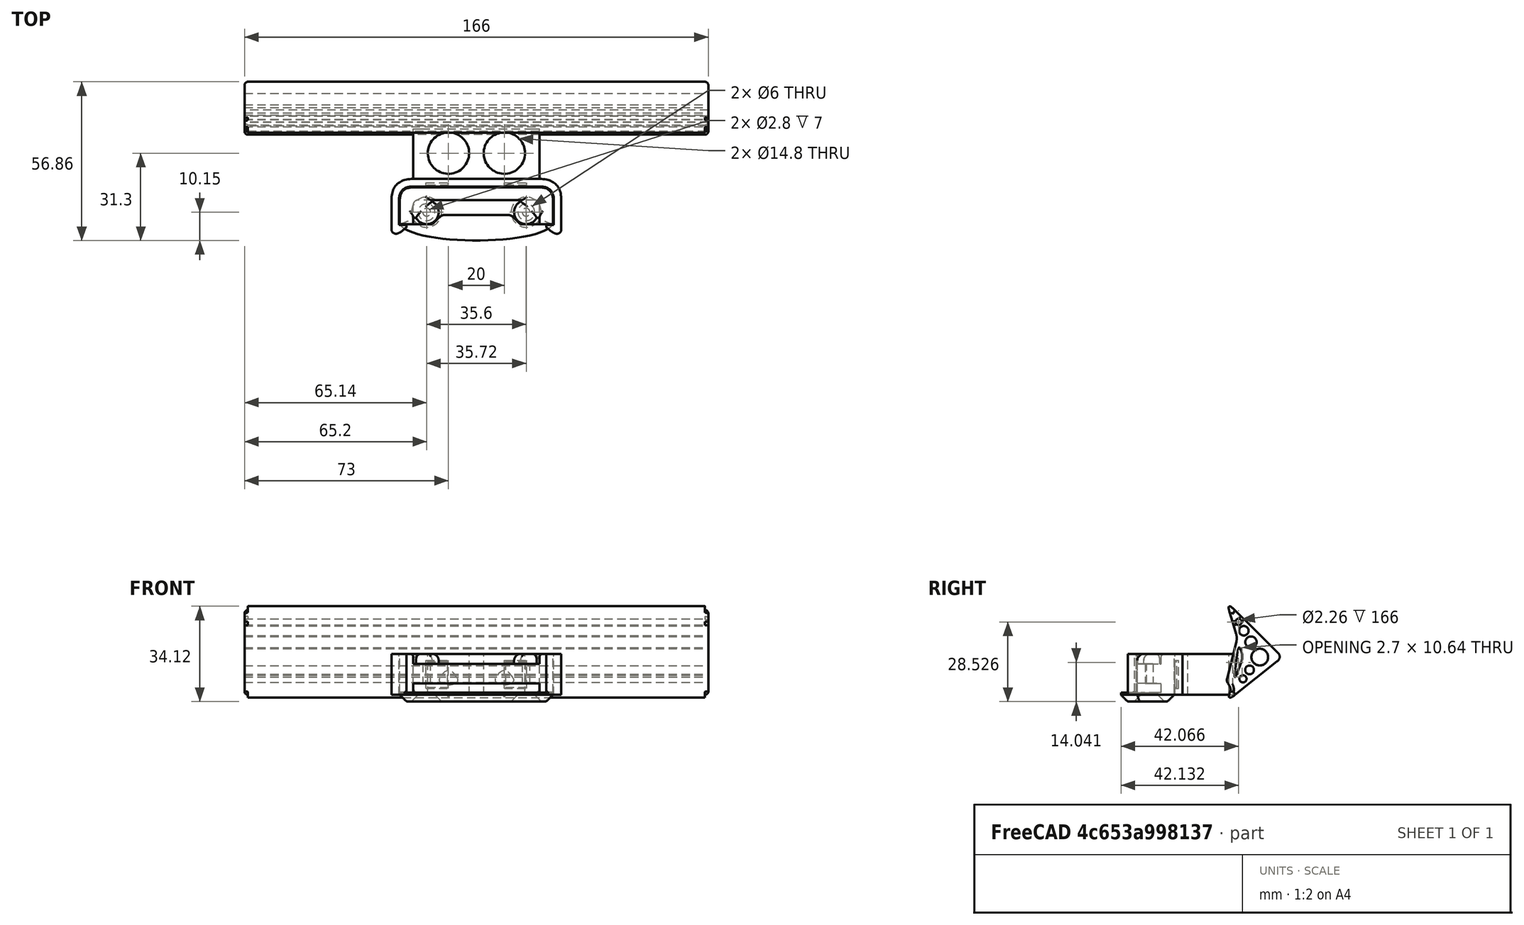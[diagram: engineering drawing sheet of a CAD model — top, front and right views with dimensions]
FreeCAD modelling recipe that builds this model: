
FCSTD DOCUMENT  (FreeCAD 0.21R0.20.1)
Label: 050
License: All rights reserved
LicenseURL: http://en.wikipedia.org/wiki/All_rights_reserved
objects: Sketcher::SketchObject×7, Part::Extrusion×7, Part::Fillet×7, Part::Box×5, Part::MultiFuse×5, Part::Cylinder×4, Part::Cut×4, Part::Chamfer×2
note: 41 computed .brp shape members not serialized (recipe doc carries the construction recipe); baked Part::Feature solids carry a one-line shape summary decoded from their .brp

FEATURE [Sketcher::SketchObject] Sketch  label="attatchmentPiece"
  FullyConstrained = true
  sketch-geometry (20):
    g0: LineSegment StartX=21.05 StartY=0 StartZ=0 EndX=21.05 EndY=-1 EndZ=0
    g1: LineSegment StartX=21.05 StartY=-1 StartZ=0 EndX=21.05 EndY=-4.3 EndZ=0
    g2: LineSegment StartX=-24.15 StartY=4.3 StartZ=0 EndX=21.05 EndY=4.3 EndZ=0
    g3: LineSegment StartX=21.05 StartY=0 StartZ=0 EndX=21.05 EndY=4.3 EndZ=0
    g4-g7: Circle x4 (B-spline internal-alignment scaffolding for g8; pole/knot coordinates omitted)
    g8: BSplineCurve PolesCount=4 KnotsCount=2 Degree=3 IsPeriodic=0
    g9: GeomPoint X=10.05 Y=-1 Z=0
    g10: GeomPoint X=14.55 Y=-4.3 Z=0
    g11: LineSegment StartX=10.05 StartY=-1 StartZ=0 EndX=-10.05 EndY=-1 EndZ=0
    g12: LineSegment StartX=14.55 StartY=-4.3 StartZ=0 EndX=21.05 EndY=-4.3 EndZ=0
    g13: LineSegment StartX=-24.15 StartY=4.3 StartZ=0 EndX=-24.15 EndY=-4.3 EndZ=0
    g14: LineSegment StartX=-13.15 StartY=-1 StartZ=0 EndX=-10.05 EndY=-1 EndZ=0
    g15: LineSegment StartX=-24.15 StartY=-4.3 StartZ=0 EndX=-19.35 EndY=-4.3 EndZ=0
    g16: LineSegment StartX=-19.35 StartY=-4.3 StartZ=0 EndX=-17.65 EndY=-4.3 EndZ=0
    g17: BSplineCurve PolesCount=4 KnotsCount=2 Degree=3 IsPeriodic=0
    g18: Circle CenterX=16.25 CenterY=0 CenterZ=0 NormalX=0 NormalY=0 NormalZ=1 AngleXU=0 Radius=1.4
    g19: Circle CenterX=-19.35 CenterY=0 CenterZ=0 NormalX=0 NormalY=0 NormalZ=1 AngleXU=0 Radius=1.4
  constraints (41):
    c: Vertical(g0)
    c: Coincident(g1,g0)
    c: Vertical(g1)
    c: Block(g0)
    c: Horizontal(g2)
    c: Vertical(g3)
    c: Coincident(g3,g2)
    c: Block(g2)
    c: Block(g3)
    c: Weight(g4) = 1
    c: Equal(g4,g5)
    c: Equal(g4,g6)
    c: Equal(g4,g7)
    c: InternalAlignment(g4-g7 -> g8) x4
    c: InternalAlignment(g9,g8)
    c: InternalAlignment(g10,g8)
    c: Block(g8)
    c: Coincident(g11,g8)
    c: Horizontal(g11)
    c: Coincident(g12,g8)
    c: Coincident(g12,g1)
    c: Horizontal(g12)
    c: Distance(g2) = 45.2
    c: Coincident(g13,g2)
    c: Vertical(g13)
    c: Horizontal(g14)
    c: Distance(g14) = 3.1
    c: Horizontal(g15)
    c: Block(g17)
    c: Coincident(g16,g15)
    c: Coincident(g16,g17)
    c: Horizontal(g16)
    c: Block(g16)
    c: Coincident(g17,g14)
    c: Block(g15)
    c: Block(g11)
    c: Block(g13)
    c: Distance(g15) = 4.8
    c: Distance(g16) = 1.7
    c: Block(g18)
    c: Block(g19)
FEATURE [Part::Extrusion] Extrude  label="attatchmentPiece001"
  Base = -> Sketch
  Dir = (0,0,1)
  DirMode = 2
  FaceMakerClass = Part::FaceMakerBullseye
  LengthFwd = 7
  LengthRev = 0
  Solid = true
  Symmetric = false
FEATURE [Sketcher::SketchObject] Sketch001  label="attatchmentPieceSurround"
  FullyConstrained = true
  sketch-geometry (18):
    g0: LineSegment StartX=25.85 StartY=-4.3 StartZ=0 EndX=21.05 EndY=-4.3 EndZ=0
    g1: LineSegment StartX=25.85 StartY=-4.3 StartZ=0 EndX=25.85 EndY=4.3 EndZ=0
    g2: LineSegment StartX=-21.05 StartY=8.9 StartZ=0 EndX=21.05 EndY=8.9 EndZ=0
    g3: Circle CenterX=21.05 CenterY=8.9 CenterZ=0 NormalX=0 NormalY=0 NormalZ=1 AngleXU=0 Radius=1
    g4: Circle CenterX=25.85 CenterY=8.9 CenterZ=0 NormalX=0 NormalY=0 NormalZ=1 AngleXU=0 Radius=1
    g5: Circle CenterX=25.85 CenterY=4.3 CenterZ=0 NormalX=0 NormalY=0 NormalZ=1 AngleXU=0 Radius=1
    g6: BSplineCurve PolesCount=3 KnotsCount=2 Degree=2 IsPeriodic=0
    g7: GeomPoint X=21.05 Y=8.9 Z=0
    g8: GeomPoint X=25.85 Y=4.3 Z=0
    g9: ArcOfCircle CenterX=19.45 CenterY=2.7 CenterZ=0 NormalX=0 NormalY=0 NormalZ=1 AngleXU=0 Radius=1.6 StartAngle=0 EndAngle=1.5708
    g10: LineSegment StartX=21.05 StartY=2.7 StartZ=0 EndX=21.05 EndY=-4.3 EndZ=0
    g11: BSplineCurve PolesCount=3 KnotsCount=2 Degree=2 IsPeriodic=0
    g12: LineSegment StartX=-28.95 StartY=-4.3 StartZ=0 EndX=-28.95 EndY=4.3 EndZ=0
    g13: LineSegment StartX=-24.15 StartY=-4.3 StartZ=0 EndX=-28.95 EndY=-4.3 EndZ=0
    g14: LineSegment StartX=-24.15 StartY=2.7 StartZ=0 EndX=-24.15 EndY=-4.3 EndZ=0
    g15: ArcOfCircle CenterX=-22.55 CenterY=2.7 CenterZ=0 NormalX=0 NormalY=0 NormalZ=1 AngleXU=0 Radius=1.6 StartAngle=1.5708 EndAngle=3.14159
    g16: LineSegment StartX=-24.15 StartY=8.9 StartZ=0 EndX=-21.05 EndY=8.9 EndZ=0
    g17: LineSegment StartX=-22.55 StartY=4.3 StartZ=0 EndX=19.45 EndY=4.3 EndZ=0
  constraints (38):
    c: Horizontal(g0)
    c: Vertical(g1)
    c: Coincident(g1,g0)
    c: Horizontal(g2)
    c: Distance(g2) = 42.1
    c: Block(g2)
    c: Coincident(g6,g2)
    c: Weight(g3) = 1
    c: Equal(g3,g4)
    c: Equal(g3,g5)
    c: Coincident(g6,g1)
    c: InternalAlignment(g3,g6)
    c: InternalAlignment(g4,g6)
    c: InternalAlignment(g5,g6)
    c: InternalAlignment(g7,g6)
    c: InternalAlignment(g8,g6)
    c: Block(g0)
    c: Block(g6)
    c: Block(g9)
    c: Coincident(g10,g9)
    c: Coincident(g10,g0)
    c: Vertical(g10)
    c: Horizontal(g13)
    c: Coincident(g12,g13)
    c: Vertical(g12)
    c: Coincident(g11,g12)
    c: Block(g12)
    c: Block(g11)
    c: Block(g15)
    c: Coincident(g14,g15)
    c: Coincident(g14,g13)
    c: Vertical(g14)
    c: Coincident(g16,g11)
    c: Coincident(g16,g2)
    c: Horizontal(g16)
    c: Coincident(g17,g15)
    c: Coincident(g17,g9)
    c: Horizontal(g17)
FEATURE [Part::Extrusion] Extrude001  label="attatchmentPieceSurround001"
  Base = -> Sketch001
  Dir = (0,0,1)
  DirMode = 2
  FaceMakerClass = Part::FaceMakerBullseye
  LengthFwd = 14.7
  LengthRev = 0
  Placement = pos=(0,0,-4.1) rot=(0,0,1;0rad)
  Solid = true
  Symmetric = false
FEATURE [Sketcher::SketchObject] Sketch002  label="attatchmentPieceEndScrewHoleCaps"
  FullyConstrained = true
  sketch-geometry (10):
    g0: ArcOfCircle CenterX=16.25 CenterY=0 CenterZ=0 NormalX=0 NormalY=0 NormalZ=1 AngleXU=0 Radius=4.3 StartAngle=2.05456 EndAngle=5.79942
    g1: LineSegment StartX=14.25 StartY=3.80657 StartZ=0 EndX=14.25 EndY=6 EndZ=0
    g2: LineSegment StartX=20.0566 StartY=-2 StartZ=0 EndX=22.25 EndY=-2 EndZ=0
    g3: LineSegment StartX=22.25 StartY=-2 StartZ=0 EndX=22.25 EndY=6 EndZ=0
    g4: LineSegment StartX=14.25 StartY=6 StartZ=0 EndX=22.25 EndY=6 EndZ=0
    g5: LineSegment StartX=-25.35 StartY=-2 StartZ=0 EndX=-25.35 EndY=6 EndZ=0
    g6: LineSegment StartX=-25.35 StartY=-2 StartZ=0 EndX=-23.1566 EndY=-2 EndZ=0
    g7: LineSegment StartX=-17.35 StartY=6 StartZ=0 EndX=-25.35 EndY=6 EndZ=0
    g8: LineSegment StartX=-17.35 StartY=3.80657 StartZ=0 EndX=-17.35 EndY=6 EndZ=0
    g9: ArcOfCircle CenterX=-19.35 CenterY=0 CenterZ=0 NormalX=0 NormalY=0 NormalZ=1 AngleXU=0 Radius=4.3 StartAngle=3.62536 EndAngle=7.37022
  constraints (25):
    c: Block(g0)
    c: Vertical(g1)
    c: Horizontal(g2)
    c: Coincident(g3,g2)
    c: Vertical(g3)
    c: Coincident(g4,g1)
    c: Horizontal(g4)
    c: Coincident(g3,g4)
    c: Block(g4)
    c: Block(g3)
    c: Coincident(g0,g1)
    c: Coincident(g0,g2)
    c: Block(g1)
    c: Block(g9)
    c: Horizontal(g6)
    c: Vertical(g8)
    c: Coincident(g7,g8)
    c: Horizontal(g7)
    c: Coincident(g5,g6)
    c: Vertical(g5)
    c: Coincident(g5,g7)
    c: Block(g7)
    c: Block(g5)
    c: Coincident(g9,g6)
    c: Coincident(g9,g8)
FEATURE [Part::Extrusion] Extrude002  label="attatchmentPieceEndScrewHoleCaps001"
  Base = -> Sketch002
  Dir = (0,0,1)
  DirMode = 2
  FaceMakerClass = Part::FaceMakerBullseye
  LengthFwd = 3.6
  LengthRev = 0
  Placement = pos=(0,0,7) rot=(0,0,1;0rad)
  Solid = true
  Symmetric = false
FEATURE [Sketcher::SketchObject] Sketch003  label="mainBumpperPieceAttatchment"
  FullyConstrained = true
  sketch-geometry (42):
    g0: Circle CenterX=28.85 CenterY=4.3 CenterZ=0 NormalX=0 NormalY=0 NormalZ=1 AngleXU=0 Radius=1
    g1: Circle CenterX=28.85 CenterY=11.9 CenterZ=0 NormalX=0 NormalY=0 NormalZ=1 AngleXU=0 Radius=1
    g2: Circle CenterX=21.05 CenterY=11.9 CenterZ=0 NormalX=0 NormalY=0 NormalZ=1 AngleXU=0 Radius=1
    g3: BSplineCurve PolesCount=3 KnotsCount=2 Degree=2 IsPeriodic=0
    g4: GeomPoint X=28.85 Y=4.3 Z=0
    g5: GeomPoint X=21.05 Y=11.9 Z=0
    g6: LineSegment StartX=-21.05 StartY=11.9 StartZ=0 EndX=21.05 EndY=11.9 EndZ=0
    g7: LineSegment StartX=28.85 StartY=4.3 StartZ=0 EndX=28.85 EndY=-4.3 EndZ=0
    g8: Circle CenterX=21.05 CenterY=9.2 CenterZ=0 NormalX=0 NormalY=0 NormalZ=1 AngleXU=0 Radius=1
    g9: Circle CenterX=26.15 CenterY=9.2 CenterZ=0 NormalX=0 NormalY=0 NormalZ=1 AngleXU=0 Radius=1
    g10: Circle CenterX=26.15 CenterY=4.3 CenterZ=0 NormalX=0 NormalY=0 NormalZ=1 AngleXU=0 Radius=1
    g11: BSplineCurve PolesCount=3 KnotsCount=2 Degree=2 IsPeriodic=0
    g12: GeomPoint X=21.05 Y=9.2 Z=0
    g13: GeomPoint X=26.15 Y=4.3 Z=0
    g14: LineSegment StartX=-21.05 StartY=9.2 StartZ=0 EndX=21.05 EndY=9.2 EndZ=0
    g15: LineSegment StartX=26.15 StartY=-4.3 StartZ=0 EndX=26.15 EndY=4.3 EndZ=0
    g16: LineSegment StartX=26.15 StartY=-4.3 StartZ=0 EndX=26.15 EndY=-4.6 EndZ=0
    g17: LineSegment StartX=23.45 StartY=-4.6 StartZ=0 EndX=26.15 EndY=-4.6 EndZ=0
    g18: LineSegment StartX=28.85 StartY=-4.3 StartZ=0 EndX=28.85 EndY=-7.9 EndZ=0
    g19: LineSegment StartX=23.45 StartY=-4.6 StartZ=0 EndX=23.45 EndY=-5.3 EndZ=0
    g20: Circle CenterX=28.85 CenterY=-7.9 CenterZ=0 NormalX=0 NormalY=0 NormalZ=1 AngleXU=0 Radius=1
    g21: Circle CenterX=26.15 CenterY=-8.2 CenterZ=0 NormalX=0 NormalY=0 NormalZ=1 AngleXU=0 Radius=1
    g22: Circle CenterX=23.45 CenterY=-5.3 CenterZ=0 NormalX=0 NormalY=0 NormalZ=1 AngleXU=0 Radius=1
    g23: BSplineCurve PolesCount=3 KnotsCount=2 Degree=2 IsPeriodic=0
    g24: GeomPoint X=28.85 Y=-7.9 Z=0
    g25: GeomPoint X=23.45 Y=-5.3 Z=0
    g26: LineSegment StartX=-21.05 StartY=9.2 StartZ=0 EndX=-24.15 EndY=9.2 EndZ=0
    g27: BSplineCurve PolesCount=3 KnotsCount=2 Degree=2 IsPeriodic=0
    g28: LineSegment StartX=-29.25 StartY=-4.3 StartZ=0 EndX=-29.25 EndY=-4.6 EndZ=0
    g29: LineSegment StartX=-29.25 StartY=-4.6 StartZ=0 EndX=-26.55 EndY=-4.6 EndZ=0
    g30: LineSegment StartX=-31.95 StartY=-4.3 StartZ=0 EndX=-31.95 EndY=-7.9 EndZ=0
    g31: LineSegment StartX=-26.55 StartY=-4.6 StartZ=0 EndX=-26.55 EndY=-5.3 EndZ=0
    g32: Circle CenterX=-31.95 CenterY=-7.9 CenterZ=0 NormalX=0 NormalY=0 NormalZ=1 AngleXU=0 Radius=1
    g33: Circle CenterX=-29.25 CenterY=-8.2 CenterZ=0 NormalX=0 NormalY=0 NormalZ=1 AngleXU=0 Radius=1
    g34: Circle CenterX=-26.55 CenterY=-5.3 CenterZ=0 NormalX=0 NormalY=0 NormalZ=1 AngleXU=0 Radius=1
    g35: BSplineCurve PolesCount=3 KnotsCount=2 Degree=2 IsPeriodic=0
    g36: GeomPoint X=-31.95 Y=-7.9 Z=0
    g37: GeomPoint X=-26.55 Y=-5.3 Z=0
    g38: LineSegment StartX=-31.95 StartY=4.3 StartZ=0 EndX=-31.95 EndY=-4.3 EndZ=0
    g39: LineSegment StartX=-29.25 StartY=-4.3 StartZ=0 EndX=-29.25 EndY=4.3 EndZ=0
    g40: BSplineCurve PolesCount=3 KnotsCount=2 Degree=2 IsPeriodic=0
    g41: LineSegment StartX=-21.05 StartY=11.9 StartZ=0 EndX=-24.15 EndY=11.9 EndZ=0
  constraints (78):
    c: Weight(g0) = 1
    c: Equal(g0,g1)
    c: Equal(g0,g2)
    c: InternalAlignment(g0,g3)
    c: InternalAlignment(g1,g3)
    c: InternalAlignment(g2,g3)
    c: InternalAlignment(g4,g3)
    c: InternalAlignment(g5,g3)
    c: Block(g3)
    c: Horizontal(g6)
    c: Vertical(g7)
    c: Block(g7)
    c: Block(g6)
    c: Weight(g8) = 1
    c: Equal(g8,g9)
    c: Equal(g8,g10)
    c: InternalAlignment(g8,g11)
    c: InternalAlignment(g9,g11)
    c: InternalAlignment(g10,g11)
    c: InternalAlignment(g12,g11)
    c: InternalAlignment(g13,g11)
    c: Horizontal(g14)
    c: Vertical(g15)
    c: Block(g11)
    c: Block(g15)
    c: Block(g14)
    c: Coincident(g16,g15)
    c: Vertical(g16)
    c: Distance(g16) = 0.3
    c: Horizontal(g17)
    c: Coincident(g17,g16)
    c: Coincident(g18,g7)
    c: Vertical(g18)
    c: Distance(g18) = 3.6
    c: Vertical(g19)
    c: Coincident(g19,g17)
    c: Coincident(g23,g18)
    c: Weight(g20) = 1
    c: Equal(g20,g21)
    c: Equal(g20,g22)
    c: Coincident(g23,g19)
    c: InternalAlignment(g20,g23)
    c: InternalAlignment(g21,g23)
    c: InternalAlignment(g22,g23)
    c: InternalAlignment(g24,g23)
    c: InternalAlignment(g25,g23)
    c: Block(g23)
    c: Horizontal(g26)
    c: Distance(g26) = 3.1
    c: Block(g27)
    c: Vertical(g38)
    c: Block(g38)
    c: Vertical(g39)
    c: Block(g40)
    c: Block(g39)
    c: Vertical(g28)
    c: Coincident(g28,g39)
    c: Coincident(g29,g28)
    c: Horizontal(g29)
    c: Vertical(g30)
    c: Coincident(g30,g38)
    c: Coincident(g31,g29)
    c: Vertical(g31)
    c: Coincident(g35,g30)
    c: Equal(g32,g33)
    c: Equal(g32,g34)
    c: Coincident(g35,g31)
    c: InternalAlignment(g32,g35)
    c: InternalAlignment(g33,g35)
    c: InternalAlignment(g34,g35)
    c: InternalAlignment(g36,g35)
    c: InternalAlignment(g37,g35)
    c: Block(g35)
    c: Coincident(g40,g26)
    c: Block(g29)
    c: Horizontal(g41)
    c: Equal(g26,g41) = 3.1
    c: Coincident(g41,g6)
FEATURE [Part::Box] Box  label="bumpperExtension"
  AttacherType = Attacher::AttachEngine3D
  Height = 14.7
  Length = 45.2
  Placement = pos=(-24.15,11.9,-4.1) rot=(0,0,1;0rad)
  Width = 18
FEATURE [Sketcher::SketchObject] Sketch004  label="bumpperMain"
  FullyConstrained = true
  Placement = pos=(0,0,0) rot=(0.57735,0.57735,0.57735;2.0944rad)
  sketch-geometry (62):
    g0: Circle CenterX=-3.12329 CenterY=2.49901 CenterZ=0 NormalX=0 NormalY=0 NormalZ=1 AngleXU=0 Radius=1
    g1: Circle CenterX=0 CenterY=0 CenterZ=0 NormalX=0 NormalY=0 NormalZ=1 AngleXU=0 Radius=1
    g2: Circle CenterX=-1.35243 CenterY=3.60648 CenterZ=0 NormalX=0 NormalY=0 NormalZ=1 AngleXU=0 Radius=1
    g3: BSplineCurve PolesCount=3 KnotsCount=2 Degree=2 IsPeriodic=0
    g4: GeomPoint X=-3.12329 Y=2.49901 Z=0
    g5: GeomPoint X=-1.35243 Y=3.60648 Z=0
    g6: Circle CenterX=-2.83953 CenterY=33.0261 CenterZ=0 NormalX=0 NormalY=0 NormalZ=1 AngleXU=0 Radius=1
    g7: Circle CenterX=0 CenterY=35.8434 CenterZ=0 NormalX=0 NormalY=0 NormalZ=1 AngleXU=0 Radius=1
    g8: Circle CenterX=-1.15771 CenterY=32.0146 CenterZ=0 NormalX=0 NormalY=0 NormalZ=1 AngleXU=0 Radius=1
    g9: BSplineCurve PolesCount=3 KnotsCount=2 Degree=2 IsPeriodic=0
    g10: GeomPoint X=-2.83953 Y=33.0261 Z=0
    g11: GeomPoint X=-1.15771 Y=32.0146 Z=0
    g12: Circle CenterX=-18.2963 CenterY=17.6904 CenterZ=0 NormalX=0 NormalY=0 NormalZ=1 AngleXU=0 Radius=1
    g13: Circle CenterX=-20 CenterY=16 CenterZ=0 NormalX=0 NormalY=0 NormalZ=1 AngleXU=0 Radius=1
    g14: Circle CenterX=-18.1259 CenterY=14.5008 CenterZ=0 NormalX=0 NormalY=0 NormalZ=1 AngleXU=0 Radius=1
    g15: BSplineCurve PolesCount=3 KnotsCount=2 Degree=2 IsPeriodic=0
    g16: GeomPoint X=-18.2963 Y=17.6904 Z=0
    g17: GeomPoint X=-18.1259 Y=14.5008 Z=0
    g18: LineSegment StartX=-18.2963 StartY=17.6904 StartZ=0 EndX=-2.83953 EndY=33.0261 EndZ=0
    g19: LineSegment StartX=-18.1259 StartY=14.5008 StartZ=0 EndX=-3.12329 EndY=2.49901 EndZ=0
    g20: Circle CenterX=-11.9527 CenterY=16 CenterZ=0 NormalX=0 NormalY=0 NormalZ=1 AngleXU=0 Radius=2.99582
    g21: Circle CenterX=-8.803 CenterY=21.3731 CenterZ=0 NormalX=0 NormalY=0 NormalZ=1 AngleXU=0 Radius=2.03939
    g22: Circle CenterX=-6.23123 CenterY=25.4475 CenterZ=0 NormalX=0 NormalY=0 NormalZ=1 AngleXU=0 Radius=1.69309
    g23: Circle CenterX=-4.38186 CenterY=28.6261 CenterZ=0 NormalX=0 NormalY=0 NormalZ=1 AngleXU=0 Radius=1.13029
    g24: Circle CenterX=-8.28033 CenterY=11.4296 CenterZ=0 NormalX=0 NormalY=0 NormalZ=1 AngleXU=0 Radius=1.57213
    g25: Circle CenterX=-5.93972 CenterY=8.22213 CenterZ=0 NormalX=0 NormalY=0 NormalZ=1 AngleXU=0 Radius=1.28743
    g26: Circle CenterX=-3.47023 CenterY=24.3665 CenterZ=0 NormalX=0 NormalY=0 NormalZ=1 AngleXU=0 Radius=1
    g27: Circle CenterX=-3.90437 CenterY=22.9307 CenterZ=0 NormalX=0 NormalY=0 NormalZ=1 AngleXU=0 Radius=1
    g28: Circle CenterX=-3.53772 CenterY=21.4762 CenterZ=0 NormalX=0 NormalY=0 NormalZ=1 AngleXU=0 Radius=1
    g29: BSplineCurve PolesCount=3 KnotsCount=2 Degree=2 IsPeriodic=0
    g30: GeomPoint X=-3.47023 Y=24.3665 Z=0
    g31: GeomPoint X=-3.53772 Y=21.4762 Z=0
    g32: LineSegment StartX=-1.15771 StartY=32.0146 StartZ=0 EndX=-3.47023 EndY=24.3665 EndZ=0
    g33: Circle CenterX=-5.41867 CenterY=17.9226 CenterZ=0 NormalX=0 NormalY=0 NormalZ=1 AngleXU=0 Radius=1
    g34: Circle CenterX=-6 CenterY=16 CenterZ=0 NormalX=0 NormalY=0 NormalZ=1 AngleXU=0 Radius=1
    g35: Circle CenterX=-5.22753 CenterY=13.9401 CenterZ=0 NormalX=0 NormalY=0 NormalZ=1 AngleXU=0 Radius=1
    g36: BSplineCurve PolesCount=3 KnotsCount=2 Degree=2 IsPeriodic=0
    g37: GeomPoint X=-5.41867 Y=17.9226 Z=0
    g38: GeomPoint X=-5.22753 Y=13.9401 Z=0
    g39: Circle CenterX=-3.98946 CenterY=10.6386 CenterZ=0 NormalX=0 NormalY=0 NormalZ=1 AngleXU=0 Radius=1
    g40: Circle CenterX=-2.58497 CenterY=6.89324 CenterZ=0 NormalX=0 NormalY=0 NormalZ=1 AngleXU=0 Radius=1
    g41: Circle CenterX=-3.11001 CenterY=10.8586 CenterZ=0 NormalX=0 NormalY=0 NormalZ=1 AngleXU=0 Radius=1
    g42: BSplineCurve PolesCount=3 KnotsCount=2 Degree=2 IsPeriodic=0
    g43: GeomPoint X=-3.98946 Y=10.6386 Z=0
    g44: GeomPoint X=-3.11001 Y=10.8586 Z=0
    g45: Circle CenterX=-1.35243 CenterY=3.60648 CenterZ=0 NormalX=0 NormalY=0 NormalZ=1 AngleXU=0 Radius=1
    g46: Circle CenterX=-1.76142 CenterY=4.69712 CenterZ=0 NormalX=0 NormalY=0 NormalZ=1 AngleXU=0 Radius=1
    g47: Circle CenterX=-1.05937 CenterY=5.79125 CenterZ=0 NormalX=0 NormalY=0 NormalZ=1 AngleXU=0 Radius=1
    g48: BSplineCurve PolesCount=3 KnotsCount=2 Degree=2 IsPeriodic=0
    g49: GeomPoint X=-1.35243 Y=3.60648 Z=0
    g50: GeomPoint X=-1.05937 Y=5.79125 Z=0
    g51: Circle CenterX=-0.519336 CenterY=6.6329 CenterZ=0 NormalX=0 NormalY=0 NormalZ=1 AngleXU=0 Radius=1
    g52: Circle CenterX=0 CenterY=7.44228 CenterZ=0 NormalX=0 NormalY=0 NormalZ=1 AngleXU=0 Radius=1
    g53: Circle CenterX=-0.244436 CenterY=8.41194 CenterZ=0 NormalX=0 NormalY=0 NormalZ=1 AngleXU=0 Radius=1
    g54: BSplineCurve PolesCount=3 KnotsCount=2 Degree=2 IsPeriodic=0
    g55: GeomPoint X=-0.519336 Y=6.6329 Z=0
    g56: GeomPoint X=-0.244436 Y=8.41194 Z=0
    g57: LineSegment StartX=-3.53772 StartY=21.4762 StartZ=0 EndX=-0.244436 EndY=8.41194 EndZ=0
    g58: LineSegment StartX=-5.22753 StartY=13.9401 StartZ=0 EndX=-3.98946 EndY=10.6386 EndZ=0
    g59: LineSegment StartX=-1.05937 StartY=5.79125 StartZ=0 EndX=-0.519336 EndY=6.6329 EndZ=0
    g60: BSplineCurve PolesCount=3 KnotsCount=2 Degree=2 IsPeriodic=0
    g61: LineSegment StartX=-4.0304 StartY=17.8099 StartZ=0 EndX=-3.11001 EndY=10.8586 EndZ=0
  constraints (96):
    c: Weight(g0) = 1
    c: Equal(g0,g1)
    c: Equal(g0,g2)
    c: InternalAlignment(g0,g3)
    c: InternalAlignment(g1,g3)
    c: InternalAlignment(g2,g3)
    c: InternalAlignment(g4,g3)
    c: InternalAlignment(g5,g3)
    c: Block(g3)
    c: Weight(g6) = 1
    c: Equal(g6,g7)
    c: Equal(g6,g8)
    c: InternalAlignment(g6,g9)
    c: InternalAlignment(g7,g9)
    c: InternalAlignment(g8,g9)
    c: InternalAlignment(g10,g9)
    c: InternalAlignment(g11,g9)
    c: Block(g9)
    c: Weight(g12) = 1
    c: Equal(g12,g13)
    c: Equal(g12,g14)
    c: InternalAlignment(g12,g15)
    c: InternalAlignment(g13,g15)
    c: InternalAlignment(g14,g15)
    c: InternalAlignment(g16,g15)
    c: InternalAlignment(g17,g15)
    c: Block(g15)
    c: Coincident(g18,g15)
    c: Coincident(g18,g9)
    c: Coincident(g19,g15)
    c: Coincident(g19,g3)
    c: Block(g25)
    c: Block(g24)
    c: Block(g20)
    c: Block(g21)
    c: Block(g22)
    c: Block(g23)
    c: Weight(g26) = 1
    c: Equal(g26,g27)
    c: Equal(g26,g28)
    c: InternalAlignment(g26,g29)
    c: InternalAlignment(g27,g29)
    c: InternalAlignment(g28,g29)
    c: InternalAlignment(g30,g29)
    c: InternalAlignment(g31,g29)
    c: Block(g29)
    c: Coincident(g32,g9)
    c: Coincident(g32,g29)
    c: Weight(g33) = 1
    c: Equal(g33,g34)
    c: Equal(g33,g35)
    c: InternalAlignment(g33,g36)
    c: InternalAlignment(g34,g36)
    c: InternalAlignment(g35,g36)
    c: InternalAlignment(g37,g36)
    c: InternalAlignment(g38,g36)
    c: Block(g36)
    c: Weight(g39) = 1
    c: Equal(g39,g40)
    c: Equal(g39,g41)
    c: InternalAlignment(g39,g42)
    c: InternalAlignment(g40,g42)
    c: InternalAlignment(g41,g42)
    c: InternalAlignment(g43,g42)
    c: InternalAlignment(g44,g42)
    c: Block(g42)
    c: Coincident(g48,g3)
    c: Weight(g45) = 1
    c: Equal(g45,g46)
    c: Equal(g45,g47)
    c: InternalAlignment(g45,g48)
    c: InternalAlignment(g46,g48)
    c: InternalAlignment(g47,g48)
    c: InternalAlignment(g49,g48)
    c: InternalAlignment(g50,g48)
    c: Block(g48)
    c: Weight(g51) = 1
    c: Equal(g51,g52)
    c: Equal(g51,g53)
    c: InternalAlignment(g51,g54)
    c: InternalAlignment(g52,g54)
    c: InternalAlignment(g53,g54)
    c: InternalAlignment(g55,g54)
    c: InternalAlignment(g56,g54)
    c: Block(g54)
    c: Coincident(g57,g29)
    c: Coincident(g57,g54)
    c: Block(g57)
    c: Coincident(g58,g36)
    c: Coincident(g58,g42)
    c: Coincident(g59,g48)
    c: Coincident(g59,g54)
    c: Block(g60)
    c: Coincident(g60,g36)
    c: Coincident(g61,g60)
    c: Coincident(g61,g42)
FEATURE [Part::Extrusion] Extrude004  label="bumpperMain001"
  Base = -> Sketch004
  Dir = (1,0,0)
  DirMode = 2
  FaceMakerClass = Part::FaceMakerBullseye
  LengthFwd = 166
  LengthRev = 0
  Placement = pos=(81.45,27.6,-6.6) rot=(0,0,1;3.14159rad)
  Solid = true
  Symmetric = false
FEATURE [Sketcher::SketchObject] Sketch005  label="attatchmentPieceBottom"
  FullyConstrained = true
  sketch-geometry (20):
    g0: LineSegment StartX=25.85 StartY=-4.3 StartZ=0 EndX=25.85 EndY=4.3 EndZ=0
    g1: LineSegment StartX=-21.05 StartY=8.9 StartZ=0 EndX=21.05 EndY=8.9 EndZ=0
    g2: Circle CenterX=21.05 CenterY=8.9 CenterZ=0 NormalX=0 NormalY=0 NormalZ=1 AngleXU=0 Radius=1
    g3: Circle CenterX=25.85 CenterY=8.9 CenterZ=0 NormalX=0 NormalY=0 NormalZ=1 AngleXU=0 Radius=1
    g4: Circle CenterX=25.85 CenterY=4.3 CenterZ=0 NormalX=0 NormalY=0 NormalZ=1 AngleXU=0 Radius=1
    g5: BSplineCurve PolesCount=3 KnotsCount=2 Degree=2 IsPeriodic=0
    g6: GeomPoint X=21.05 Y=8.9 Z=0
    g7: GeomPoint X=25.85 Y=4.3 Z=0
    g8: BSplineCurve PolesCount=3 KnotsCount=2 Degree=2 IsPeriodic=0
    g9: LineSegment StartX=-28.95 StartY=-4.3 StartZ=0 EndX=-28.95 EndY=4.3 EndZ=0
    g10: LineSegment StartX=-24.15 StartY=8.9 StartZ=0 EndX=-21.05 EndY=8.9 EndZ=0
    g11: Circle CenterX=-19.41 CenterY=0 CenterZ=0 NormalX=0 NormalY=0 NormalZ=1 AngleXU=0 Radius=3
    g12: Circle CenterX=16.3103 CenterY=0 CenterZ=0 NormalX=0 NormalY=0 NormalZ=1 AngleXU=0 Radius=3
    g13-g16: Circle x4 (B-spline internal-alignment scaffolding for g17; pole/knot coordinates omitted)
    g17: BSplineCurve PolesCount=4 KnotsCount=2 Degree=3 IsPeriodic=0
    g18: GeomPoint X=-28.95 Y=-4.3 Z=0
    g19: GeomPoint X=25.85 Y=-4.3 Z=0
  constraints (36):
    c: Vertical(g0)
    c: Horizontal(g1)
    c: Distance(g1) = 42.1
    c: Block(g1)
    c: Coincident(g5,g1)
    c: Weight(g2) = 1
    c: Equal(g2,g3)
    c: Equal(g2,g4)
    c: Coincident(g5,g0)
    c: InternalAlignment(g2,g5)
    c: InternalAlignment(g3,g5)
    c: InternalAlignment(g4,g5)
    c: InternalAlignment(g6,g5)
    c: InternalAlignment(g7,g5)
    c: Block(g5)
    c: Vertical(g9)
    c: Coincident(g8,g9)
    c: Block(g9)
    c: Block(g8)
    c: Coincident(g10,g8)
    c: Coincident(g10,g1)
    c: Horizontal(g10)
    c: PointOnObject(g12,g-1)
    c: PointOnObject(g11,g-1)
    c: Block(g11)
    c: Block(g12)
    c: Coincident(g17,g9)
    c: Weight(g13) = 1
    c: Equal(g13,g14)
    c: Equal(g13,g15)
    c: Equal(g13,g16)
    c: Coincident(g17,g0)
    c: InternalAlignment(g13-g16 -> g17) x4
    c: InternalAlignment(g18,g17)
    c: InternalAlignment(g19,g17)
    c: Block(g17)
FEATURE [Part::Extrusion] Extrude005  label="removeFromMainBumpperPieceAttatchment"
  Base = -> Sketch005
  Dir = (0,0,1)
  DirMode = 2
  FaceMakerClass = Part::FaceMakerBullseye
  LengthFwd = 3.2
  LengthRev = 0
  Placement = pos=(0,0,-6.2) rot=(0,0,1;0rad)
  Solid = true
  Symmetric = false
FEATURE [Part::Extrusion] Extrude006  label="mainBumpperPieceAttatchment001"
  Base = -> Sketch003
  Dir = (0,0,1)
  DirMode = 2
  FaceMakerClass = Part::FaceMakerBullseye
  LengthFwd = 14.7
  LengthRev = 0
  Placement = pos=(0,0,-4.1) rot=(0,0,1;0rad)
  Solid = true
  Symmetric = false
FEATURE [Part::Cylinder] Cylinder  label="removeFromBumpperExtension"
  Angle = 360
  AttacherType = Attacher::AttachEngine3D
  FirstAngle = 0
  Height = 20
  Placement = pos=(8.45,21.15,-8) rot=(0,0,1;0rad)
  Radius = 7.4
  SecondAngle = 0
FEATURE [Part::Cylinder] Cylinder001  label="removeFromBumpperExtension001"
  Angle = 360
  AttacherType = Attacher::AttachEngine3D
  FirstAngle = 0
  Height = 20
  Placement = pos=(-11.55,21.15,-8) rot=(0,0,1;0rad)
  Radius = 7.4
  SecondAngle = 0
FEATURE [Part::MultiFuse] Fusion  label="removeFromBumpperExtension002"
  Shapes = -> [Cylinder,Cylinder001]
FEATURE [Part::Cylinder] Cylinder002  label="removeFromBumpperExtension004"
  Angle = 360
  AttacherType = Attacher::AttachEngine3D
  FirstAngle = 0
  Height = 20
  Placement = pos=(8.45,21.15,-8) rot=(0,0,1;0rad)
  Radius = 7.4
  SecondAngle = 0
FEATURE [Part::Cylinder] Cylinder003  label="removeFromBumpperExtension005"
  Angle = 360
  AttacherType = Attacher::AttachEngine3D
  FirstAngle = 0
  Height = 20
  Placement = pos=(-11.55,21.15,-8) rot=(0,0,1;0rad)
  Radius = 7.4
  SecondAngle = 0
FEATURE [Part::MultiFuse] Fusion001  label="removeFromBumpperMain"
  Shapes = -> [Cylinder002,Cylinder003]
FEATURE [Part::Cut] Cut  label="bumpperExtension001"
  Base = -> Box
  Tool = -> Fusion
FEATURE [Part::Fillet] Fillet  label="bumpperExtension002"
  Base = -> Cut
  Edges = 4 edges r=3: [Edge2,Edge4,Edge9,Edge14]
FEATURE [Part::Box] Box001  label="bumpperExtensionBumpHole"
  AttacherType = Attacher::AttachEngine3D
  Height = 10
  Length = 8
  Placement = pos=(8.45,9.2,-1.8) rot=(0,0,1;0rad)
  Width = 1.3
FEATURE [Part::Box] Box002  label="bumpperExtensionBumpHole001"
  AttacherType = Attacher::AttachEngine3D
  Height = 10
  Length = 8
  Placement = pos=(-19.55,9.2,-1.8) rot=(0,0,1;0rad)
  Width = 1.3
FEATURE [Part::Box] Box003  label="attatchmentPieceSurroundBump"
  AttacherType = Attacher::AttachEngine3D
  Height = 9.2
  Length = 7.2
  Placement = pos=(8.85,8.9,-1.4) rot=(0,0,1;0rad)
  Width = 1.3
FEATURE [Part::Box] Box004  label="attatchmentPieceSurroundBump001"
  AttacherType = Attacher::AttachEngine3D
  Height = 9.2
  Length = 7.2
  Placement = pos=(-19.15,8.9,-1.4) rot=(0,0,1;0rad)
  Width = 1.3
FEATURE [Part::MultiFuse] Fusion002  label="attatchmentPieceSurroundBump002"
  Placement = pos=(0,-0.4,0) rot=(0,0,1;0rad)
  Shapes = -> [Box004,Box003]
FEATURE [Part::MultiFuse] Fusion003  label="bumpperExtensionBumpHole002"
  Shapes = -> [Box002,Box001]
FEATURE [Part::Cut] Cut002  label="mainBumpperPieceAttatchment002"
  Base = -> Extrude006
  Tool = -> Fusion003
FEATURE [Part::Fillet] Fillet003  label="attatchmentPieceEndScrewHoleCaps002"
  Base = -> Extrude002
  Edges = 6 edges r=2.4: [Edge4,Edge7,Edge15,Edge25,Edge28,Edge30]
FEATURE [Part::Fillet] Fillet004  label="attatchmentPieceSurround002"
  Base = -> Extrude001
  Edges = 3 edges r=1.2: [Edge19,Edge25,Edge31]
FEATURE [Part::Fillet] Fillet006  label="mainBumpperPieceAttatchment003"
  Base = -> Cut002
  Edges = 2 edges r=1.6: [Edge2,Edge55]
FEATURE [Sketcher::SketchObject] Sketch006  label="attatchmentPieceBottom002"
  FullyConstrained = true
  sketch-geometry (20):
    g0: LineSegment StartX=25.85 StartY=-4.3 StartZ=0 EndX=25.85 EndY=4.3 EndZ=0
    g1: LineSegment StartX=-21.05 StartY=8.9 StartZ=0 EndX=21.05 EndY=8.9 EndZ=0
    g2: Circle CenterX=21.05 CenterY=8.9 CenterZ=0 NormalX=0 NormalY=0 NormalZ=1 AngleXU=0 Radius=1
    g3: Circle CenterX=25.85 CenterY=8.9 CenterZ=0 NormalX=0 NormalY=0 NormalZ=1 AngleXU=0 Radius=1
    g4: Circle CenterX=25.85 CenterY=4.3 CenterZ=0 NormalX=0 NormalY=0 NormalZ=1 AngleXU=0 Radius=1
    g5: BSplineCurve PolesCount=3 KnotsCount=2 Degree=2 IsPeriodic=0
    g6: GeomPoint X=21.05 Y=8.9 Z=0
    g7: GeomPoint X=25.85 Y=4.3 Z=0
    g8: BSplineCurve PolesCount=3 KnotsCount=2 Degree=2 IsPeriodic=0
    g9: LineSegment StartX=-28.95 StartY=-4.3 StartZ=0 EndX=-28.95 EndY=4.3 EndZ=0
    g10: LineSegment StartX=-24.15 StartY=8.9 StartZ=0 EndX=-21.05 EndY=8.9 EndZ=0
    g11: Circle CenterX=-19.41 CenterY=0 CenterZ=0 NormalX=0 NormalY=0 NormalZ=1 AngleXU=0 Radius=3
    g12: Circle CenterX=16.3103 CenterY=0 CenterZ=0 NormalX=0 NormalY=0 NormalZ=1 AngleXU=0 Radius=3
    g13-g16: Circle x4 (B-spline internal-alignment scaffolding for g17; pole/knot coordinates omitted)
    g17: BSplineCurve PolesCount=4 KnotsCount=2 Degree=3 IsPeriodic=0
    g18: GeomPoint X=-28.95 Y=-4.3 Z=0
    g19: GeomPoint X=25.85 Y=-4.3 Z=0
  constraints (36):
    c: Vertical(g0)
    c: Horizontal(g1)
    c: Distance(g1) = 42.1
    c: Block(g1)
    c: Coincident(g5,g1)
    c: Weight(g2) = 1
    c: Equal(g2,g3)
    c: Equal(g2,g4)
    c: Coincident(g5,g0)
    c: InternalAlignment(g2,g5)
    c: InternalAlignment(g3,g5)
    c: InternalAlignment(g4,g5)
    c: InternalAlignment(g6,g5)
    c: InternalAlignment(g7,g5)
    c: Block(g5)
    c: Vertical(g9)
    c: Coincident(g8,g9)
    c: Block(g9)
    c: Block(g8)
    c: Coincident(g10,g8)
    c: Coincident(g10,g1)
    c: Horizontal(g10)
    c: PointOnObject(g12,g-1)
    c: PointOnObject(g11,g-1)
    c: Block(g11)
    c: Block(g12)
    c: Coincident(g17,g9)
    c: Weight(g13) = 1
    c: Equal(g13,g14)
    c: Equal(g13,g15)
    c: Equal(g13,g16)
    c: Coincident(g17,g0)
    c: InternalAlignment(g13-g16 -> g17) x4
    c: InternalAlignment(g18,g17)
    c: InternalAlignment(g19,g17)
    c: Block(g17)
FEATURE [Part::Extrusion] Extrude007  label="attatchmentPieceBottom003"
  Base = -> Sketch006
  Dir = (0,0,1)
  DirMode = 2
  FaceMakerClass = Part::FaceMakerBullseye
  LengthFwd = 3.2
  LengthRev = 0
  Placement = pos=(0,0,-6.5) rot=(0,0,1;0rad)
  Solid = true
  Symmetric = false
FEATURE [Part::Cut] Cut003  label="mainBumpperPieceAttatchment004"
  Base = -> Fillet006
  Tool = -> Extrude005
FEATURE [Part::Chamfer] Chamfer
  Base = -> Extrude007
  Edges = 2 edges r=2.4: [Edge23,Edge26]
FEATURE [Part::Chamfer] Chamfer001  label="attatchmentPieceBottom004"
  Base = -> Chamfer
  Edges = 7 edges r=2.4: [Edge14,Edge15,Edge16,Edge17,Edge18,Edge19,Edge20]
FEATURE [Part::Fillet] Fillet007  label="attatchmentPieceBottom005"
  Base = -> Chamfer001
  Edges = 7 edges r=1.2: [Edge1,Edge2,Edge3,Edge4,Edge5,Edge6,Edge7]
FEATURE [Part::MultiFuse] Fusion007  label="attatchment"
  Shapes = -> [Fillet007,Fillet004,Fillet003,Fusion002,Extrude]
FEATURE [Part::Cut] Cut001  label="bumpperMain002"
  Base = -> Extrude004
  Tool = -> Fusion001
FEATURE [Part::Fillet] Fillet001
  Base = -> Cut001
  Edges = 11 edges r=1.2: [Edge4,Edge7,Edge10,Edge30,Edge31,Edge32,Edge33,Edge34,Edge35,Edge36,Edge37]
FEATURE [Part::Fillet] Fillet002  label="bumpperMain003"
  Base = -> Fillet001
  Edges = 11 edges r=1.2: [Edge4,Edge9,Edge13,Edge14,Edge15,Edge16,Edge17,Edge18,Edge19,Edge20,Edge21]
